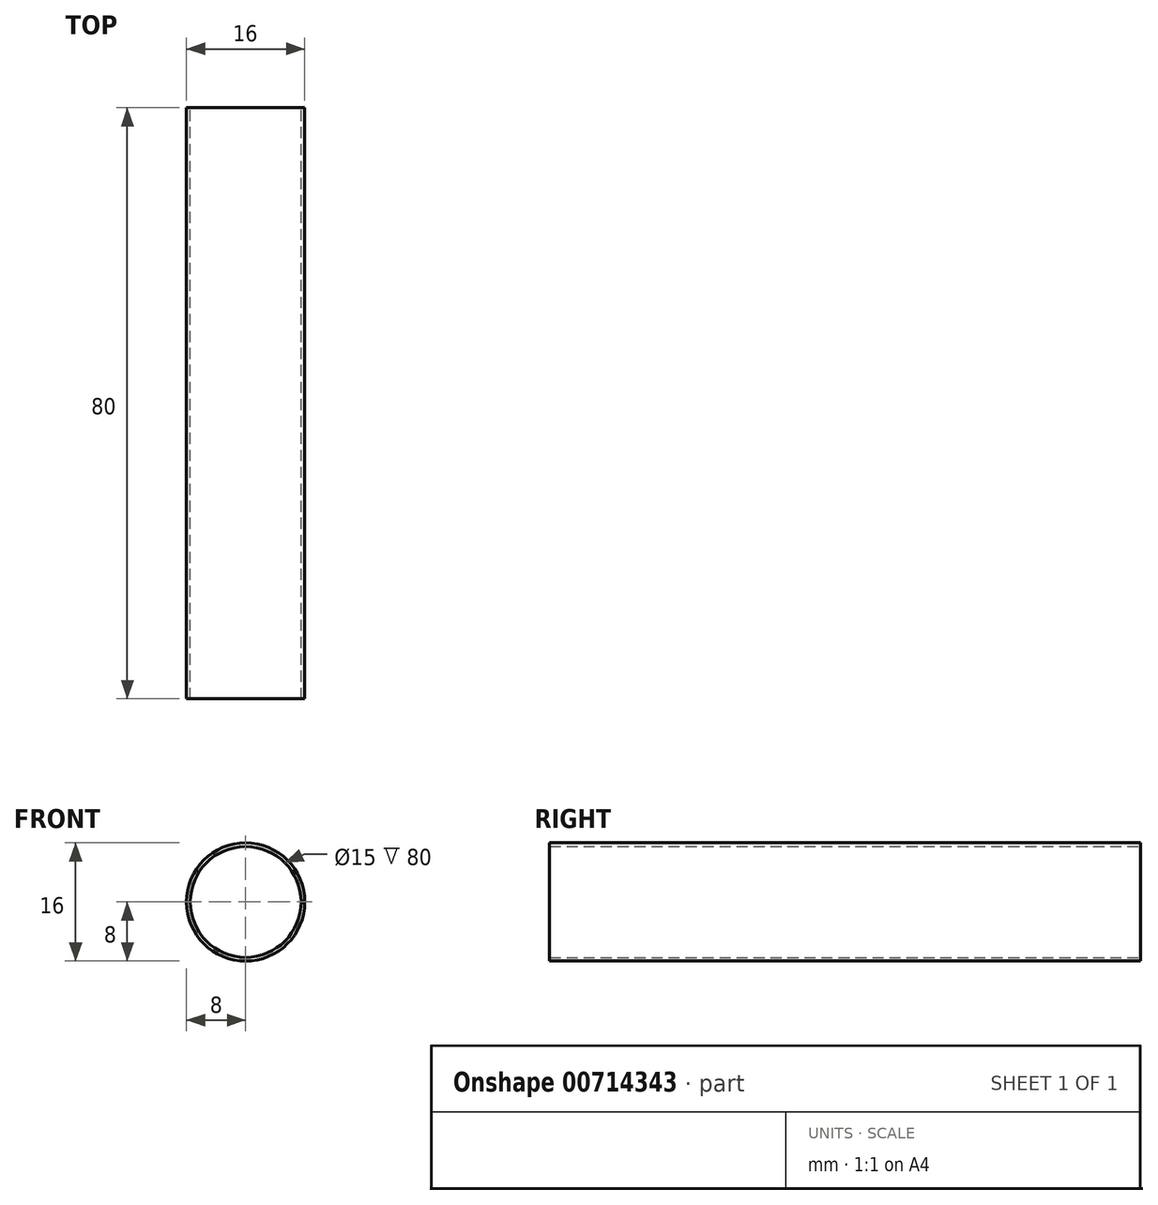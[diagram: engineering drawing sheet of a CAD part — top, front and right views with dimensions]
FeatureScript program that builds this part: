
annotation { "Feature Type Name" : "Feature", "Feature Type Description" : "" }
export const myFeature = defineFeature(function(context is Context, id is Id, definition is map)
    precondition{}
    {
        {
            var Q0;
            Q0=qCreatedBy(makeId("Front.planeOp"),FACE);
            var sketch = newSketch(context, id + "F0", { "sketchPlane" : qUnion([Q0])});
            skCircle(sketch, "E0", {"center": v(0, 0) * mm, "radius": 8 * mm});
            skCircle(sketch, "E1", {"center": v(0, 0) * mm, "radius": 7.5 * mm});
            skSolve(sketch);
        }
        {
            var Q0;
            Q0 = qSketchRegion(id + "F0", true);
            extrude(context, id + "F1", {"entities" : qUnion([Q0]), "depth" : 80 * mm, "offsetDistance" : 25 * mm});
        }
    });
